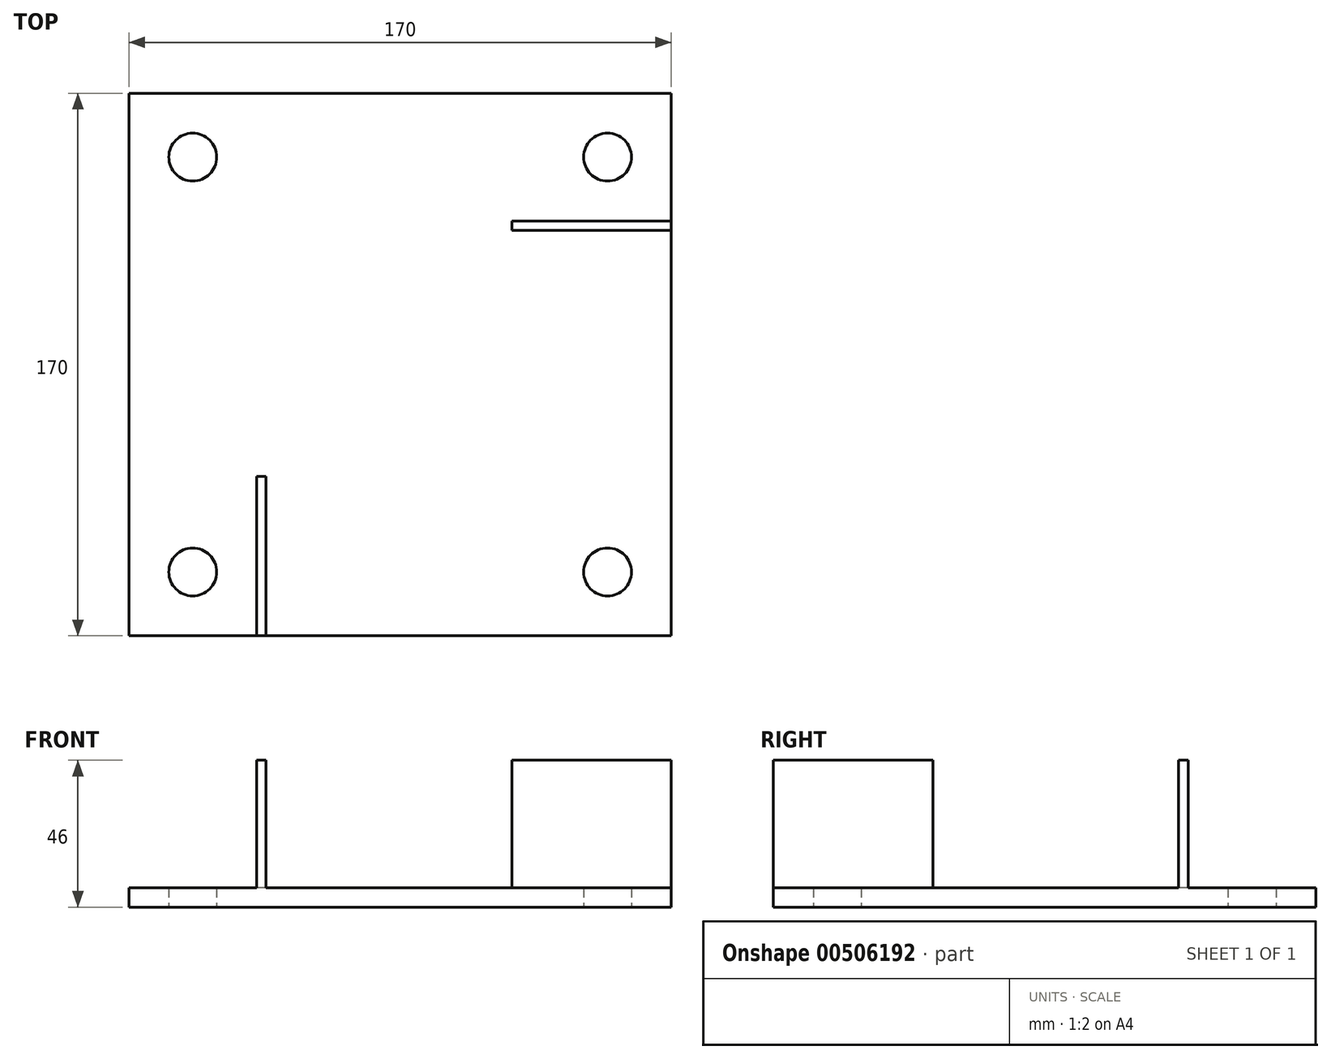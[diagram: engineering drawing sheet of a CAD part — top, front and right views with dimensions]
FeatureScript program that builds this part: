
annotation { "Feature Type Name" : "Feature", "Feature Type Description" : "" }
export const myFeature = defineFeature(function(context is Context, id is Id, definition is map)
    precondition{}
    {
        {
            var Q0;
            Q0=qCreatedBy(makeId("Top.planeOp"),FACE);
            var sketch = newSketch(context, id + "F0", { "sketchPlane" : qUnion([Q0])});
            skPoint(sketch, "E0.middle", {"position": v(0, 0) * mm});
            skCircle(sketch, "E1", {"center": v(-65, 65) * mm, "radius": 7.5 * mm});
            skCircle(sketch, "E2", {"center": v(65, 65) * mm, "radius": 7.5 * mm});
            skCircle(sketch, "E3", {"center": v(65, -65) * mm, "radius": 7.5 * mm});
            skCircle(sketch, "E4", {"center": v(-65, -65) * mm, "radius": 7.5 * mm});
            skLineSegment(sketch, "E5.bottom", {"start": v(85, 85) * mm, "end": v(-85, 85) * mm});
            skLineSegment(sketch, "E5.top", {"start": v(85, -85) * mm, "end": v(-85, -85) * mm});
            skLineSegment(sketch, "E5.left", {"start": v(85, 85) * mm, "end": v(85, -85) * mm});
            skLineSegment(sketch, "E5.right", {"start": v(-85, 85) * mm, "end": v(-85, -85) * mm});
            skSolve(sketch);
        }
        {
            var Q0;
            Q0 = qSketchRegion(id + "F0", true);
            extrude(context, id + "F1", {"entities" : qUnion([Q0]), "depth" : 6 * mm});
        }
        {
            var Q0;
            Q0=makeQuery(id+"F1.opExtrude","CAP_FACE",FACE,{"disambiguationData":[OSD([sQuery(id+"F0.wireOp",EDGE,"E1"),sQuery(id+"F0.wireOp",EDGE,"E2"),sQuery(id+"F0.wireOp",EDGE,"E3"),sQuery(id+"F0.wireOp",EDGE,"E4"),sQuery(id+"F0.wireOp",EDGE,"E5.bottom"),sQuery(id+"F0.wireOp",EDGE,"E5.top"),sQuery(id+"F0.wireOp",EDGE,"E5.left"),sQuery(id+"F0.wireOp",EDGE,"E5.right")])],"isStart":false});
            var sketch = newSketch(context, id + "F2", { "sketchPlane" : qUnion([Q0])});
            skLineSegment(sketch, "E6.bottom", {"start": v(-42, -35) * mm, "end": v(-45, -35) * mm});
            skLineSegment(sketch, "E6.top", {"start": v(-42, -85) * mm, "end": v(-45, -85) * mm});
            skLineSegment(sketch, "E6.left", {"start": v(-42, -35) * mm, "end": v(-42, -85) * mm});
            skLineSegment(sketch, "E6.right", {"start": v(-45, -35) * mm, "end": v(-45, -85) * mm});
            skLineSegment(sketch, "E7.bottom", {"start": v(35, 45) * mm, "end": v(85, 45) * mm});
            skLineSegment(sketch, "E7.top", {"start": v(35, 42) * mm, "end": v(85, 42) * mm});
            skLineSegment(sketch, "E7.left", {"start": v(35, 45) * mm, "end": v(35, 42) * mm});
            skLineSegment(sketch, "E7.right", {"start": v(85, 45) * mm, "end": v(85, 42) * mm});
            skSolve(sketch);
        }
        {
            var Q0;
            Q0 = qSketchRegion(id + "F2", true);
            extrude(context, id + "F3", {"entities" : qUnion([Q0]), "operationType" : NewBodyOperationType.ADD, "depth" : 40 * mm, "offsetDistance" : 25 * mm});
        }
    });
